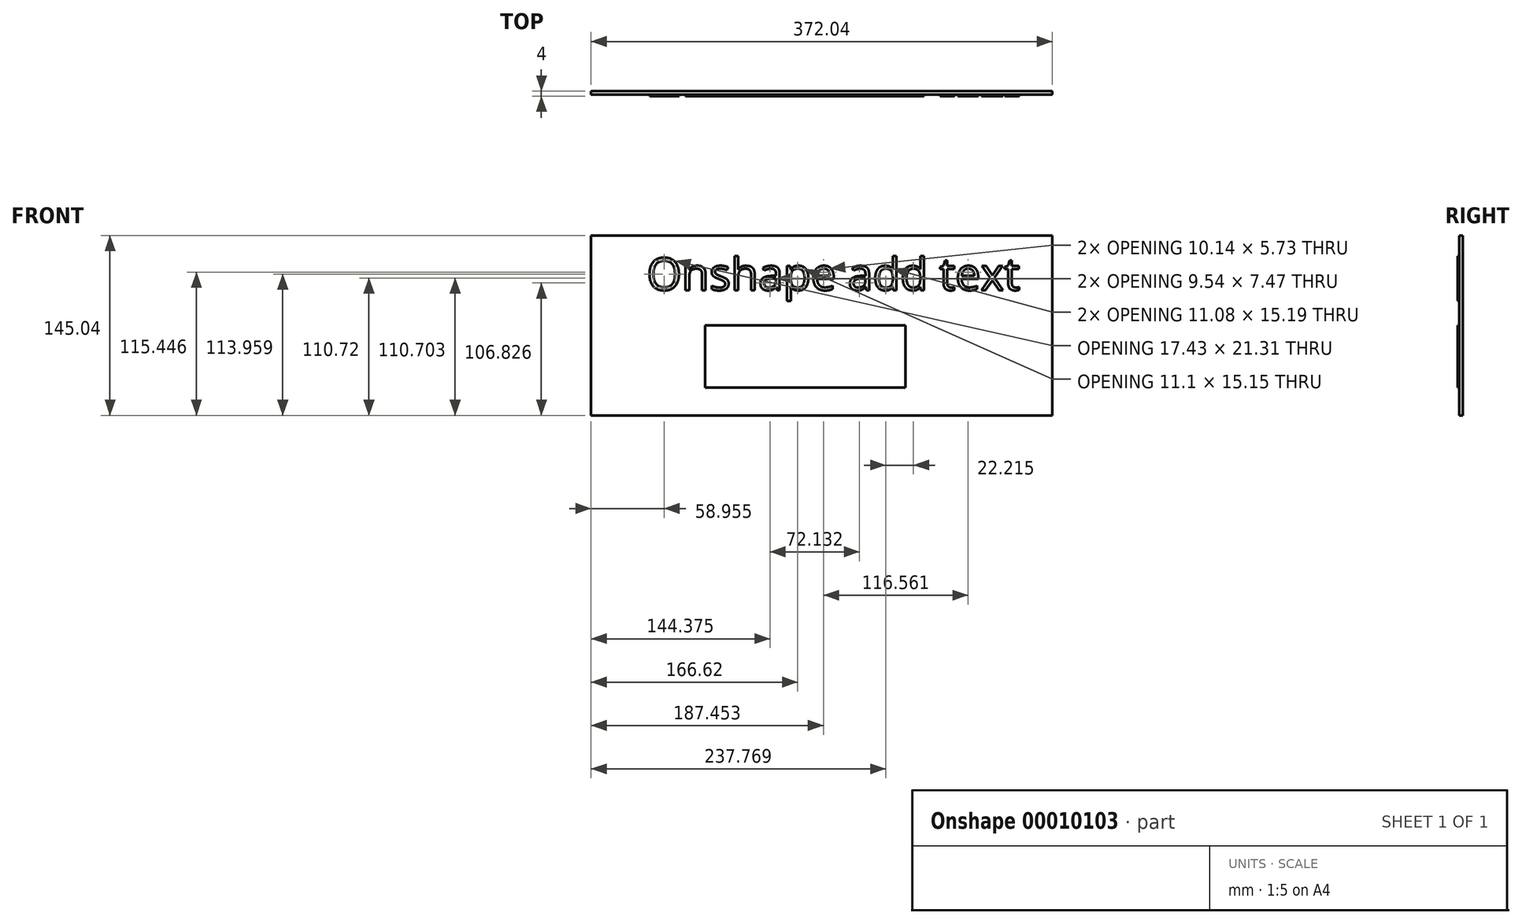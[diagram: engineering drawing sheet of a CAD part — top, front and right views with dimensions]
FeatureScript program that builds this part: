
annotation { "Feature Type Name" : "Feature", "Feature Type Description" : "" }
export const myFeature = defineFeature(function(context is Context, id is Id, definition is map)
    precondition{}
    {
        {
            var Q0;
            Q0=qCreatedBy(makeId("Front.planeOp"),FACE);
            var sketch = newSketch(context, id + "F0", { "sketchPlane" : qUnion([Q0])});
            skLineSegment(sketch, "E0.rect.bottom", {"start": v(186.02, -72.52) * mm, "end": v(-186.02, -72.52) * mm});
            skLineSegment(sketch, "E0.rect.top", {"start": v(186.02, 72.52) * mm, "end": v(-186.02, 72.52) * mm});
            skLineSegment(sketch, "E0.rect.left", {"start": v(186.02, -72.52) * mm, "end": v(186.02, 72.52) * mm});
            skLineSegment(sketch, "E0.rect.right", {"start": v(-186.02, -72.52) * mm, "end": v(-186.02, 72.52) * mm});
            skPoint(sketch, "E0.rect.middle", {"position": v(0, 0) * mm});
            skSolve(sketch);
        }
        {
            var Q0;
            Q0 = qSketchRegion(id + "F0", true);
            extrude(context, id + "F1", {"entities" : qUnion([Q0]), "depth" : 3 * mm});
        }
        {
            var Q0;
            Q0=makeQuery(id+"F1.opExtrude","CAP_FACE",FACE,{"disambiguationData":[OSD([sQuery(id+"F0.wireOp",EDGE,"E0.rect.bottom"),sQuery(id+"F0.wireOp",EDGE,"E0.rect.top"),sQuery(id+"F0.wireOp",EDGE,"E0.rect.left"),sQuery(id+"F0.wireOp",EDGE,"E0.rect.right")])],"isStart":false});
            var sketch = newSketch(context, id + "F2", { "sketchPlane" : qUnion([Q0])});
            skLineSegment(sketch, "E1", {"start": v(-49.44, 17.6) * mm, "end": v(50.44, 17.6) * mm, "construction": true});
            skArc(sketch, "E2", {"start": v(51.2, -31.09) * mm, "mid": v(1.57, -4.45) * mm, "end": v(-45.7, -35.09) * mm, "construction": true});
            skText(sketch, "E3", { "text": "Onshape add text", "fontName": "OpenSans-Regular.ttf"});
            const initialGuessF2  = {"E3": [-0.14118, 0.0285, 1, 0, 0.0261]};
            skSetInitialGuess(sketch, initialGuessF2);
            skSolve(sketch);
        }
        {
            var Q0;
            Q0 = qSketchRegion(id + "F2", true);
            extrude(context, id + "F3", {"entities" : qUnion([Q0]), "depth" : 1 * mm});
        }
        {
            var Q0;
            {var subQ0=sQuery(id+"F0.wireOp",EDGE,"E0.rect.bottom");var subQ1=sQuery(id+"F0.wireOp",EDGE,"E0.rect.top");var subQ2=sQuery(id+"F0.wireOp",EDGE,"E0.rect.left");var subQ3=sQuery(id+"F0.wireOp",EDGE,"E0.rect.right");Q0=makeQuery(id+"F3.boolean.opBoolean","SPLIT",FACE,{"disambiguationData":[TD([makeQuery(id+"F1.opExtrude","SWEPT_FACE",FACE,{"disambiguationData":[OSD([subQ0])]})])],"derivedFrom":makeQuery(id+"F1.opExtrude","CAP_FACE",FACE,{"disambiguationData":[OSD([subQ0,subQ1,subQ2,subQ3])],"isStart":false})});}
            var sketch = newSketch(context, id + "F4", { "sketchPlane" : qUnion([Q0])});
            skPoint(sketch, "E4", {"position": v(-151.28, -18.46) * mm});
            skSolve(sketch);
        }
        {
            var Q0;
            Q0=makeQuery(id+"F4.imprint","IMPRINT",FACE,{"disambiguationData":[TD([[makeQuery(id+"F4.imprint","IMPRINT",EDGE,{"derivedFrom":makeQuery(id+"F1.opExtrude","CAP_EDGE",EDGE,{"disambiguationData":[OSD([sQuery(id+"F0.wireOp",EDGE,"E0.rect.bottom")])],"isStart":false})}),-1.0]])]});
            var sketch = newSketch(context, id + "F5", { "sketchPlane" : qUnion([Q0])});
            skLineSegment(sketch, "E5.rect.bottom", {"start": v(67.67, -50) * mm, "end": v(-93.93, -50) * mm});
            skLineSegment(sketch, "E5.rect.top", {"start": v(67.67, 0) * mm, "end": v(-93.93, 0) * mm});
            skLineSegment(sketch, "E5.rect.left", {"start": v(67.67, -50) * mm, "end": v(67.67, 0) * mm});
            skLineSegment(sketch, "E5.rect.right", {"start": v(-93.93, -50) * mm, "end": v(-93.93, 0) * mm});
            skPoint(sketch, "E5.rect.middle", {"position": v(-13.13, -25) * mm});
            skSolve(sketch);
        }
        {
            var Q0;
            Q0 = qSketchRegion(id + "F5", true);
            extrude(context, id + "F6", {"entities" : qUnion([Q0]), "depth" : 1 * mm});
        }
        {
            var Q0;
            Q0=makeQuery(id+"F4.imprint","IMPRINT",FACE,{"disambiguationData":[TD([[makeQuery(id+"F4.imprint","IMPRINT",EDGE,{"derivedFrom":makeQuery(id+"F1.opExtrude","CAP_EDGE",EDGE,{"disambiguationData":[OSD([sQuery(id+"F0.wireOp",EDGE,"E0.rect.bottom")])],"isStart":false})}),-1.0]])]});
            var sketch = newSketch(context, id + "F7", { "sketchPlane" : qUnion([Q0])});
            skLineSegment(sketch, "E6.bottom", {"start": v(-105.26, 0) * mm, "end": v(0, 0) * mm});
            skLineSegment(sketch, "E6.top", {"start": v(-105.26, -60.75) * mm, "end": v(0, -60.75) * mm});
            skLineSegment(sketch, "E6.left", {"start": v(-105.26, 0) * mm, "end": v(-105.26, -60.75) * mm});
            skLineSegment(sketch, "E6.right", {"start": v(0, 0) * mm, "end": v(0, -60.75) * mm});
            skSolve(sketch);
        }
        {
            var Q0;
            Q0=sQuery(id+"F7.wireOp",EDGE,"E6.top");
            var Q1;
            Q1=sQuery(id+"F7.wireOp",EDGE,"E6.left");
            var Q2;
            Q2=sQuery(id+"F7.wireOp",EDGE,"E6.bottom");
            var Q3;
            Q3=sQuery(id+"F7.wireOp",EDGE,"E6.right");
            extrude(context, id + "F8", {"bodyType" : ToolBodyType.SURFACE, "surfaceEntities" : qUnion([Q0, Q1, Q2, Q3]), "depth" : 15 * mm});
        }
    });
